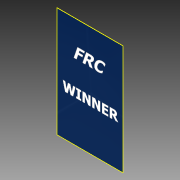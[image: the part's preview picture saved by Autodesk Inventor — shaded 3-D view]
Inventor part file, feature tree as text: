
AUTODESK INVENTOR PART (.ipt)
format: ipt  version: 2014 (Build 180170000, 170)  size: 80,384 bytes
history: native  units: in
note: dims shown in document units (in); Inventor stores cm internally (conversion verified against a paired STEP export)
features: sketch x2, extrude x1
ambient origin geometry x8: Origin, YZ Plane, XZ Plane, XY Plane, X Axis, Y Axis, Z Axis, Center Point
bodies: Solid1 (feature_tree)
feature tree (3):
  extrude  "Extrusion1"  Depth=60.0in
  sketch  "Sketch2"  dims[d2=0.2in d3=0.0in]
  sketch  "Sketch1"  dims[d0=36.0in d1=60.0in]
